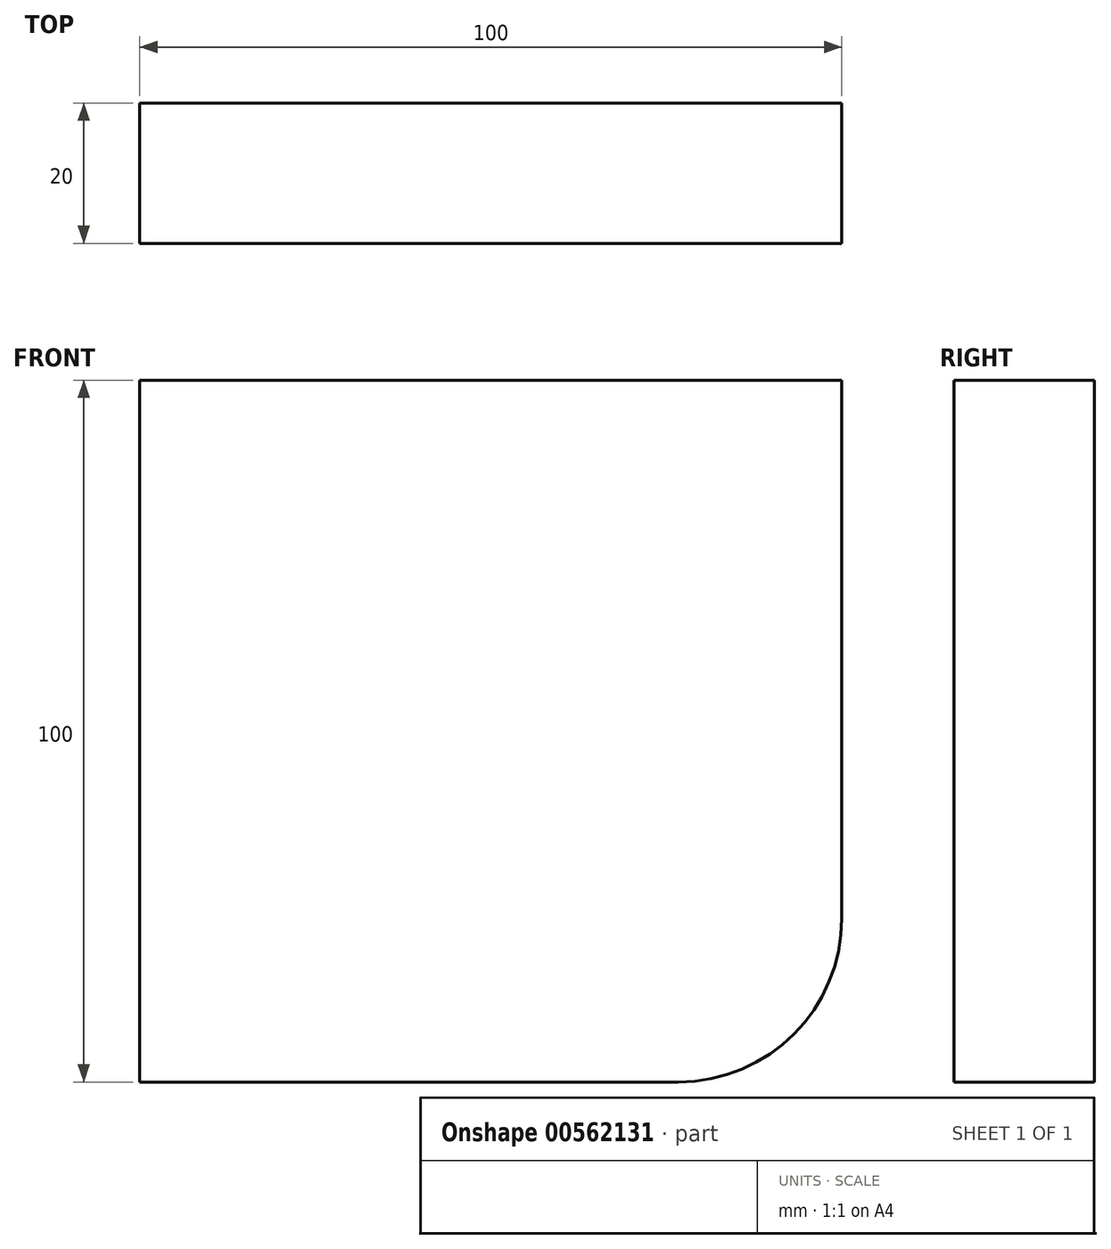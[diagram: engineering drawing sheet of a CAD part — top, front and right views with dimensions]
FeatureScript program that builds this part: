
annotation { "Feature Type Name" : "Feature", "Feature Type Description" : "" }
export const myFeature = defineFeature(function(context is Context, id is Id, definition is map)
    precondition{}
    {
        {
            var Q0;
            Q0=qCreatedBy(makeId("Front.planeOp"),FACE);
            var sketch = newSketch(context, id + "F0", { "sketchPlane" : qUnion([Q0])});
            skLineSegment(sketch, "E0.bottom", {"start": v(50, 50) * mm, "end": v(-50, 50) * mm});
            skLineSegment(sketch, "E0.top", {"start": v(50, -50) * mm, "end": v(-50, -50) * mm});
            skLineSegment(sketch, "E0.left", {"start": v(50, 50) * mm, "end": v(50, -50) * mm});
            skLineSegment(sketch, "E0.right", {"start": v(-50, 50) * mm, "end": v(-50, -50) * mm});
            skPoint(sketch, "E0.middle", {"position": v(0, 0) * mm});
            skSolve(sketch);
        }
        {
            var Q0;
            Q0=makeQuery(id+"F0.imprint","IMPRINT",FACE,{"disambiguationData":[TD([[makeQuery(id+"F0.imprint","IMPRINT",EDGE,{"derivedFrom":sQuery(id+"F0.wireOp",EDGE,"E0.bottom")}),1.0]])]});
            extrude(context, id + "F1", {"entities" : qUnion([Q0]), "depth" : 20 * mm, "offsetDistance" : 25.4 * mm});
        }
        {
            var Q0;
            Q0=makeQuery(id+"F1.opExtrude","SWEPT_EDGE",EDGE,{"disambiguationData":[OSD([sQuery(id+"F0.wireOp",EDGE,"E0.top"),sQuery(id+"F0.wireOp",EDGE,"E0.left")])]});
            fillet(context, id + "F2", {"entities" : qUnion([Q0]), "radius" : 23.3 * mm, "tangentPropagation" : true, "allowEdgeOverflow" : false});
        }
        {
            var Q0;
            Q0=qCreatedBy(makeId("Front.planeOp"),FACE);
            var sketch = newSketch(context, id + "F3", { "sketchPlane" : qUnion([Q0])});
            skCircle(sketch, "E1", {"center": v(24.66, -23.76) * mm, "radius": 15.13 * mm});
            skSolve(sketch);
        }
        {
            var Q0;
            Q0 = qSketchRegion(id + "F3", true);
            extrude(context, id + "F4", {"entities" : qUnion([Q0]), "operationType" : NewBodyOperationType.ADD, "depth" : 20 * mm, "offsetDistance" : 25.4 * mm});
        }
    });
